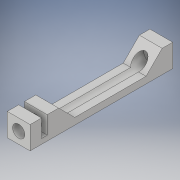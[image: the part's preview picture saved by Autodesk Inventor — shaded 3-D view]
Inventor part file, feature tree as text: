
AUTODESK INVENTOR PART (.ipt)
format: ipt  version: 2019.4 (Build 234330000, 330)  size: 287,744 bytes
history: native  units: in
note: dims shown in document units (in); Inventor stores cm internally (conversion verified against a paired STEP export)
features: extrude x5, sketch x5
ambient origin geometry x8: Origin, YZ Plane, XZ Plane, XY Plane, X Axis, Y Axis, Z Axis, Center Point
bodies: Solid1 (feature_tree)
feature tree (10):
  extrude  "Extrusion1"  Depth=1.9685in
  extrude  "Extrusion2"  Depth=0.315in
  extrude  "Extrusion3"  Depth=0.0787in
  extrude  "Extrusion4"  Depth=0.2441in TaperAngle=0.0deg
  extrude  "Extrusion5"  Depth=0.1575in
  sketch  "Sketch1"  dims[d0=0.315in d1=1.9685in]
  sketch  "Sketch2"  dims[d2=0.315in d3=0.0in d4=0.1693in]
  sketch  "Sketch3"  dims[d5=0.1575in d6=0.0in d8=0.0787in]
  sketch  "Sketch4"  dims[d9=0.1575in d10=0.2441in d11=0.0in]
  sketch  "Sketch5"  dims[d12=1.5748in d13=0.0in d14=0.1575in d15=0.315in d16=135.0deg d17=0.9843in d18=135.0deg d19=1.5748in d20=0.0in]
